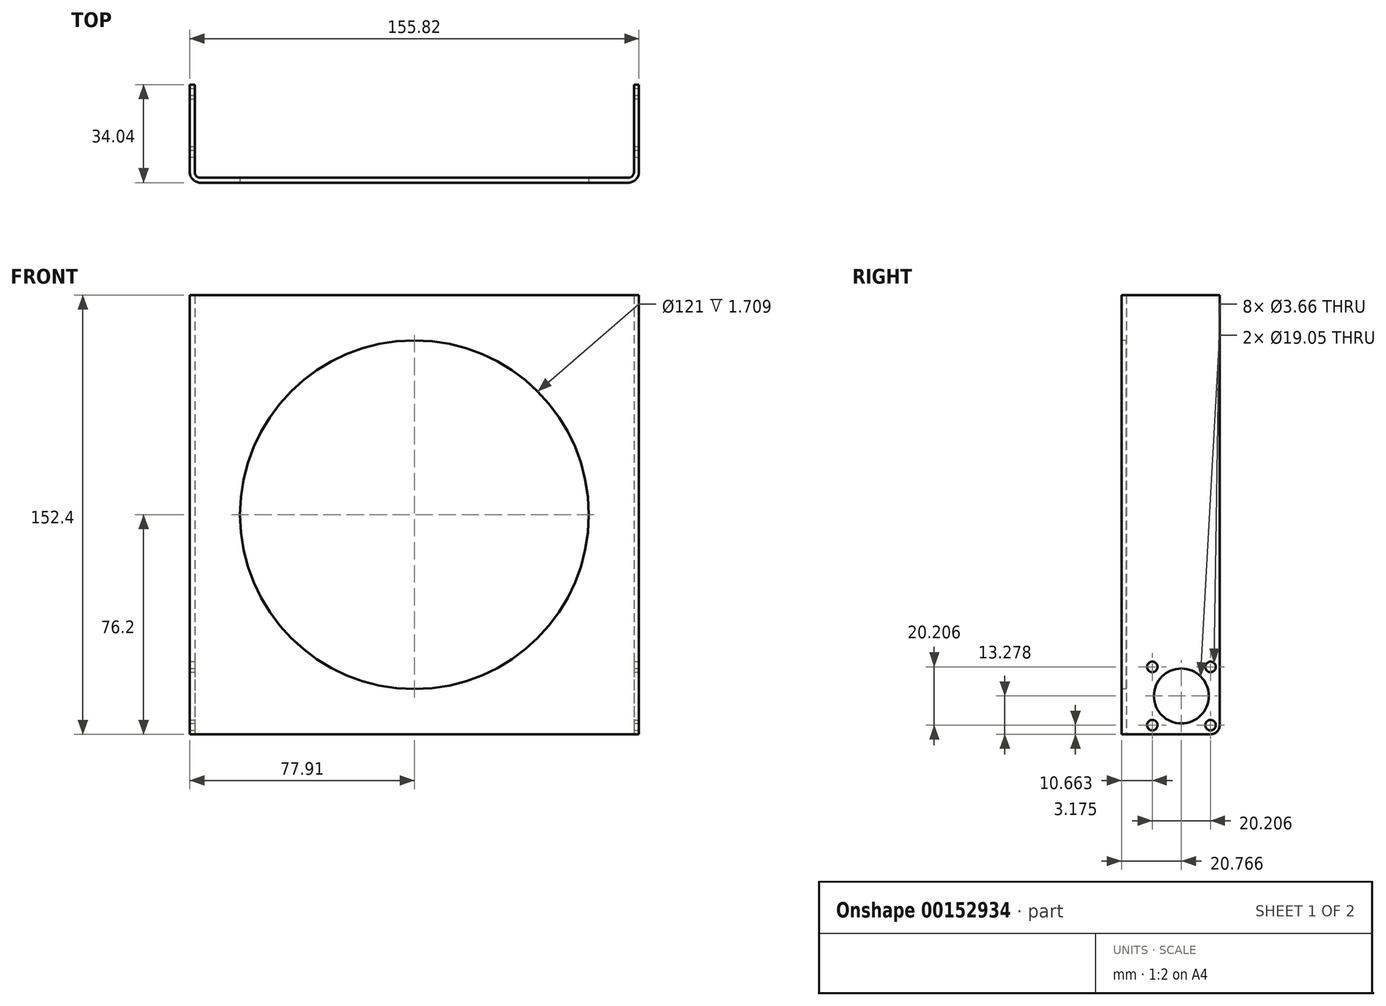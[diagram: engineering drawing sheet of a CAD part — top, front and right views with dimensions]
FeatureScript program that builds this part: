
annotation { "Feature Type Name" : "Feature", "Feature Type Description" : "" }
export const myFeature = defineFeature(function(context is Context, id is Id, definition is map)
    precondition{}
    {
        {
            var Q0;
            Q0=qCreatedBy(makeId("Top.planeOp"),FACE);
            var sketch = newSketch(context, id + "F0", { "sketchPlane" : qUnion([Q0])});
            skLineSegment(sketch, "E0.bottom", {"start": v(0, 0) * mm, "end": v(-152.4, 0) * mm});
            skLineSegment(sketch, "E0.top", {"start": v(1.7, -1.7) * mm, "end": v(-154.1, -1.7) * mm});
            skLineSegment(sketch, "E1.top", {"start": v(-152.4, 32.33) * mm, "end": v(-154.1, 32.33) * mm});
            skLineSegment(sketch, "E1.left", {"start": v(-152.4, 0) * mm, "end": v(-152.4, 32.33) * mm});
            skLineSegment(sketch, "E1.right", {"start": v(-154.1, -1.7) * mm, "end": v(-154.1, 32.33) * mm});
            skLineSegment(sketch, "E2.top", {"start": v(0, 32.33) * mm, "end": v(1.7, 32.33) * mm});
            skLineSegment(sketch, "E2.left", {"start": v(0, 0) * mm, "end": v(0, 32.33) * mm});
            skLineSegment(sketch, "E2.right", {"start": v(1.7, -1.7) * mm, "end": v(1.7, 32.33) * mm});
            skLineSegment(sketch, "E3", {"start": v(-76.2, 0) * mm, "end": v(-76.2, -1.7) * mm, "construction": true});
            skSolve(sketch);
        }
        {
            var Q0;
            Q0=qSketchRegion(id+"F0",true);
            extrude(context, id + "F1", {"entities" : qUnion([Q0]), "depth" : 152.4 * mm});
        }
        {
            var Q0;
            Q0=makeQuery(id+"FcdIcV9w6YY9zah_1.opExtrude","CAP_EDGE",EDGE,{"disambiguationData":[OSD([sQuery(id+"FU7sgaIbCbRhSfr_1.wireOp",EDGE,"F29Sxc5V-O2cl-wjtz-gx5o-reTTBG7m1pNU.top")])],"isStart":true});
            var Q1;
            Q1=makeQuery(id+"FcdIcV9w6YY9zah_1.opExtrude","CAP_EDGE",EDGE,{"disambiguationData":[OSD([sQuery(id+"FU7sgaIbCbRhSfr_1.wireOp",EDGE,"yv2bQU74-Eht6-uYuo-WBF2-3C4kyuaz0slr.top")])],"isStart":true});
            var Q2;
            Q2=makeQuery(id+"F1.opExtrude","SWEPT_EDGE",EDGE,{"disambiguationData":[OSD([sQuery(id+"F0.wireOp",EDGE,"E0.bottom"),sQuery(id+"F0.wireOp",EDGE,"E2.left")])]});
            var Q3;
            Q3=makeQuery(id+"F1.opExtrude","SWEPT_EDGE",EDGE,{"disambiguationData":[OSD([sQuery(id+"F0.wireOp",EDGE,"E0.bottom"),sQuery(id+"F0.wireOp",EDGE,"E1.left")])]});
            fillet(context, id + "F2", {"entities" : qUnion([Q0, Q1, Q2, Q3]), "radius" : 1.98 * mm, "tangentPropagation" : true, "allowEdgeOverflow" : false});
        }
        {
            var Q0;
            Q0=makeQuery(id+"FkwQQH4eT4IjhdK_1.opExtrude","CAP_EDGE",EDGE,{"disambiguationData":[OSD([sQuery(id+"FvDFSbhwMPyTNrQ_1.wireOp",EDGE,"223FG13h-YrEq-unoX-9EOi-DwKLLmwbrteD.top")])],"isStart":false});
            var Q1;
            Q1=makeQuery(id+"F1.opExtrude","SWEPT_EDGE",EDGE,{"disambiguationData":[OSD([sQuery(id+"F0.wireOp",EDGE,"E0.top"),sQuery(id+"F0.wireOp",EDGE,"E2.right")])]});
            var Q2;
            Q2=makeQuery(id+"F1.opExtrude","SWEPT_EDGE",EDGE,{"disambiguationData":[OSD([sQuery(id+"F0.wireOp",EDGE,"E0.top"),sQuery(id+"F0.wireOp",EDGE,"E1.right")])]});
            var Q3;
            Q3=makeQuery(id+"F2kHonbXZaQoFrR_1.opExtrude","CAP_EDGE",EDGE,{"disambiguationData":[OSD([sQuery(id+"FsAbJG8AZOSwdHE_1.wireOp",EDGE,"WRaIy3id-o2EU-qHqw-IwdC-eHQZRSiK4KpF.bottom")])],"isStart":false});
            fillet(context, id + "F3", {"entities" : qUnion([Q0, Q1, Q2, Q3]), "radius" : 3.7 * mm, "tangentPropagation" : true, "allowEdgeOverflow" : false});
        }
        {
            var Q0;
            Q0=makeQuery(id+"F1.opExtrude","CAP_EDGE",EDGE,{"disambiguationData":[OSD([sQuery(id+"F0.wireOp",EDGE,"E1.top")])],"isStart":true});
            var Q1;
            Q1=makeQuery(id+"F1.opExtrude","CAP_EDGE",EDGE,{"disambiguationData":[OSD([sQuery(id+"F0.wireOp",EDGE,"E2.top")])],"isStart":true});
            fillet(context, id + "F4", {"entities" : qUnion([Q0, Q1]), "radius" : 3.17 * mm, "tangentPropagation" : true, "allowEdgeOverflow" : false});
        }
        {
            var Q0;
            Q0=makeQuery(id+"F1.opExtrude","SWEPT_FACE",FACE,{"disambiguationData":[OSD([sQuery(id+"F0.wireOp",EDGE,"E2.right")])]});
            var sketch = newSketch(context, id + "F5", { "sketchPlane" : qUnion([Q0])});
            skLineSegment(sketch, "E4.bottom", {"start": v(29.16, 3.18) * mm, "end": v(8.95, 3.17) * mm, "construction": true});
            skLineSegment(sketch, "E4.top", {"start": v(29.16, 23.38) * mm, "end": v(8.95, 23.38) * mm, "construction": true});
            skLineSegment(sketch, "E4.left", {"start": v(29.16, 3.18) * mm, "end": v(29.16, 23.38) * mm, "construction": true});
            skLineSegment(sketch, "E4.right", {"start": v(8.95, 3.17) * mm, "end": v(8.95, 23.38) * mm, "construction": true});
            skPoint(sketch, "E4.middle", {"position": v(19.06, 13.28) * mm});
            skCircle(sketch, "E5", {"center": v(19.06, 13.28) * mm, "radius": 9.53 * mm});
            skCircle(sketch, "E6", {"center": v(19.06, 13.28) * mm, "radius": 11.11 * mm, "construction": true});
            skCircle(sketch, "E7", {"center": v(29.16, 3.18) * mm, "radius": 3.18 * mm, "construction": true});
            skCircle(sketch, "E8", {"center": v(29.16, 23.38) * mm, "radius": 1.83 * mm});
            skCircle(sketch, "E9", {"center": v(29.16, 3.18) * mm, "radius": 1.83 * mm});
            skCircle(sketch, "E10", {"center": v(8.95, 3.17) * mm, "radius": 1.83 * mm});
            skCircle(sketch, "E11", {"center": v(8.95, 23.38) * mm, "radius": 1.83 * mm});
            skSolve(sketch);
        }
        {
            var Q0;
            Q0 = qSketchRegion(id + "F5", true);
            var Q1;
            Q1=makeQuery(id+"F1.opExtrude","SWEPT_FACE",FACE,{"disambiguationData":[OSD([sQuery(id+"F0.wireOp",EDGE,"E1.right")])]});
            extrude(context, id + "F6", {"entities" : qUnion([Q0]), "operationType" : NewBodyOperationType.REMOVE, "endBound" : BoundingType.UP_TO_SURFACE, "oppositeDirection" : true, "endBoundEntityFace" : qUnion([Q1]), "depth" : 25.4 * mm});
        }
        {
            var Q0;
            Q0=makeQuery(id+"F1.opExtrude","SWEPT_FACE",FACE,{"disambiguationData":[OSD([sQuery(id+"F0.wireOp",EDGE,"E0.top")])]});
            var sketch = newSketch(context, id + "F7", { "sketchPlane" : qUnion([Q0])});
            skLineSegment(sketch, "E12", {"start": v(-76.2, 152.4) * mm, "end": v(-76.2, 0) * mm, "construction": true});
            skLineSegment(sketch, "E13.bottom", {"start": v(-19.32, 131.41) * mm, "end": v(-133.08, 131.41) * mm, "construction": true});
            skLineSegment(sketch, "E13.top", {"start": v(-19.32, 20.99) * mm, "end": v(-133.08, 20.99) * mm, "construction": true});
            skLineSegment(sketch, "E13.left", {"start": v(-19.32, 131.41) * mm, "end": v(-19.32, 20.99) * mm, "construction": true});
            skLineSegment(sketch, "E13.right", {"start": v(-133.08, 131.41) * mm, "end": v(-133.08, 20.99) * mm, "construction": true});
            skPoint(sketch, "E13.middle", {"position": v(-76.2, 76.2) * mm});
            skCircle(sketch, "E14", {"center": v(-76.2, 76.2) * mm, "radius": 60.5 * mm});
            skSolve(sketch);
        }
        {
            var Q0;
            Q0 = qSketchRegion(id + "F7", true);
            var Q1;
            Q1=makeQuery(id+"F1.opExtrude","SWEPT_FACE",FACE,{"disambiguationData":[OSD([sQuery(id+"F0.wireOp",EDGE,"E0.bottom")])]});
            extrude(context, id + "F8", {"entities" : qUnion([Q0]), "operationType" : NewBodyOperationType.REMOVE, "endBound" : BoundingType.UP_TO_SURFACE, "oppositeDirection" : true, "endBoundEntityFace" : qUnion([Q1]), "depth" : 25.4 * mm});
        }
    });
